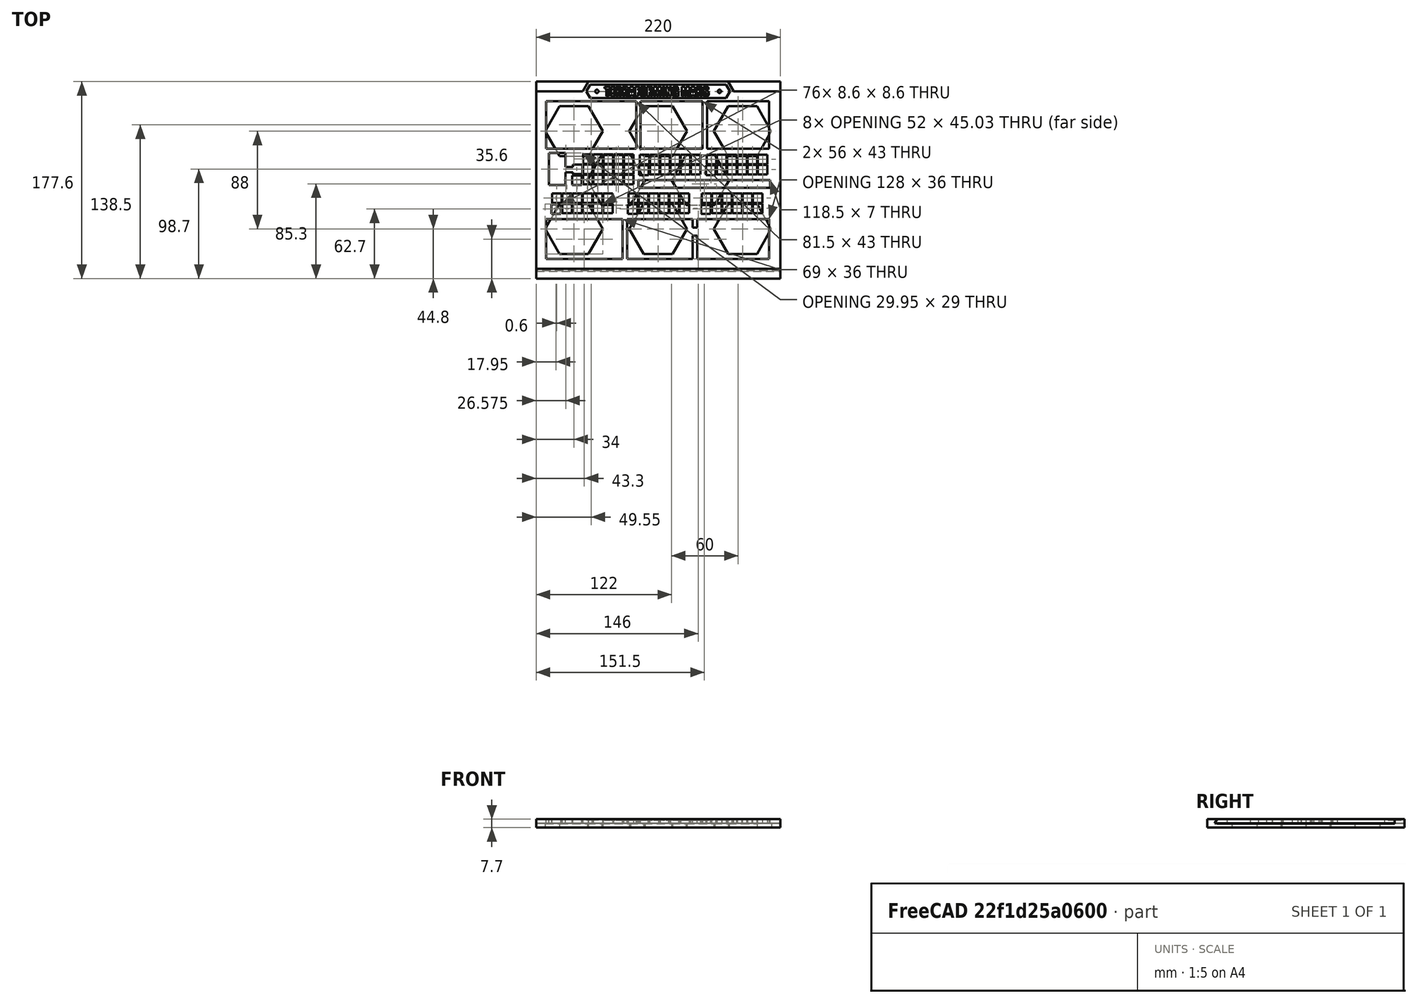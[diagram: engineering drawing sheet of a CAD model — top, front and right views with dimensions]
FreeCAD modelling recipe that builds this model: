
FCSTD DOCUMENT  (FreeCAD 0.21R33668 +26 (Git))
Label: overlay-full-v6
License: All rights reserved
LicenseURL: https://en.wikipedia.org/wiki/All_rights_reserved
objects: Sketcher::SketchObject×11, PartDesign::Pad×9, PartDesign::Pocket×5, Part::Feature×2, Part::Part2DObjectPython×2, PartDesign::Body×2, Mesh::Feature×1, Part::Refine×1, PartDesign::FeatureBase×1, Part::Extrusion×1
note: 48 computed .brp shape members not serialized (recipe doc carries the construction recipe); baked Part::Feature solids carry a one-line shape summary decoded from their .brp

FEATURE [Mesh::Feature] Terraforming_Mars_overlay
FEATURE [Part::Feature] Terraforming_Mars_overlay001
  shape: bbox 208 x 148 x 3.7 mm, 1736 faces, 0 solids (baked)
FEATURE [Part::Feature] Terraforming_Mars_overlay001_solid  label="Terraforming_Mars_overlay001 (Solid)"
  shape: bbox 208 x 148 x 3.7 mm, 1736 faces (baked)
FEATURE [Part::Refine] Terraforming_Mars_overlay001_solid001  label="Terraforming_Mars_overlay001 (Solid)001"
  Source = -> Terraforming_Mars_overlay001_solid
FEATURE [PartDesign::FeatureBase] BaseFeature
  BaseFeature = -> Terraforming_Mars_overlay001_solid001
FEATURE [Sketcher::SketchObject] Sketch
  ExternalGeometry = -> [BaseFeature]
  FullyConstrained = true
  MapMode = 5
  Placement = pos=(0,0,3.7) rot=(0,0,1;0rad)
  Support = -> [BaseFeature]
  sketch-geometry (8):
    g0: LineSegment StartX=6 StartY=154 StartZ=0 EndX=214 EndY=154 EndZ=0
    g1: LineSegment StartX=214 StartY=154 StartZ=0 EndX=214 EndY=6 EndZ=0
    g2: LineSegment StartX=214 StartY=6 StartZ=0 EndX=6 EndY=6 EndZ=0
    g3: LineSegment StartX=6 StartY=6 StartZ=0 EndX=6 EndY=154 EndZ=0
    g4: LineSegment StartX=0 StartY=160 StartZ=0 EndX=220 EndY=160 EndZ=0
    g5: LineSegment StartX=220 StartY=160 StartZ=0 EndX=220 EndY=0 EndZ=0
    g6: LineSegment StartX=220 StartY=0 StartZ=0 EndX=0 EndY=0 EndZ=0
    g7: LineSegment StartX=0 StartY=0 StartZ=0 EndX=0 EndY=160 EndZ=0
  constraints (22):
    c: Coincident(g0,g1)
    c: Coincident(g1,g2)
    c: Coincident(g2,g3)
    c: Coincident(g3,g0)
    c: Horizontal(g0)
    c: Horizontal(g2)
    c: Vertical(g1)
    c: Vertical(g3)
    c: Coincident(g0,g-3)
    c: Coincident(g1,g-4)
    c: Coincident(g4,g5)
    c: Coincident(g5,g6)
    c: Coincident(g6,g7)
    c: Coincident(g7,g4)
    c: Horizontal(g4)
    c: Horizontal(g6)
    c: Vertical(g5)
    c: Vertical(g7)
    c: DistanceX(g4,g0) = 6
    c: DistanceX(g0,g4) = 6
    c: DistanceY(g0,g4) = 6
    c: DistanceY(g5,g1) = 6
FEATURE [PartDesign::Pad] Pad
  BaseFeature = -> BaseFeature
  Direction = (0,0,1)
  Length = 10
  Length2 = 10
  Profile = -> Sketch
  ReferenceAxis = -> Sketch [N_Axis]
  Type = 3
  UpToFace = -> BaseFeature [Face1]
FEATURE [Sketcher::SketchObject] Sketch001
  ExternalGeometry = -> [Pad]
  FullyConstrained = true
  MapMode = 5
  Placement = pos=(0,0,3.7) rot=(0,0,1;0rad)
  Support = -> [Pad]
  sketch-geometry (5):
    g0: GeomPoint X=110 Y=160 Z=0
    g1: LineSegment StartX=42 StartY=160 StartZ=0 EndX=47.0807 EndY=168.8 EndZ=0
    g2: LineSegment StartX=47.0807 StartY=168.8 StartZ=0 EndX=172.919 EndY=168.8 EndZ=0
    g3: LineSegment StartX=172.919 StartY=168.8 StartZ=0 EndX=178 EndY=160 EndZ=0
    g4: LineSegment StartX=178 StartY=160 StartZ=0 EndX=42 EndY=160 EndZ=0
  constraints (13):
    c: Symmetric(g-3,g-3,g0)
    c: Coincident(g1,g2)
    c: Horizontal(g2)
    c: Coincident(g2,g3)
    c: Coincident(g3,g4)
    c: Coincident(g4,g1)
    c: Angle(g1,g4,g1) = 2.0944
    c: Angle(g4,g3,g3) = 2.0944
    c: DistanceY(g1,g1) = 8.8
    c: PointOnObject(g1,g-3)
    c: DistanceX(g-3,g1) = 42
    c: DistanceX(g3,g-3) = 42
    c: PointOnObject(g3,g-3)
FEATURE [PartDesign::Pad] Pad001
  BaseFeature = -> Pad
  Direction = (0,0,1)
  Length = 10
  Length2 = 10
  Profile = -> Sketch001
  ReferenceAxis = -> Sketch001 [N_Axis]
  Type = 3
  UpToFace = -> Pad [Face2]
FEATURE [Sketcher::SketchObject] Sketch002
  ExternalGeometry = -> [Pad001]
  FullyConstrained = true
  MapMode = 5
  Placement = pos=(0,0,3.7) rot=(0,0,1;0rad)
  Support = -> [Pad001]
  sketch-geometry (7):
    g0: GeomPoint X=110 Y=160 Z=0
    g1: LineSegment StartX=45.2332 StartY=160 StartZ=0 EndX=48.6973 EndY=166 EndZ=0
    g2: LineSegment StartX=48.6973 StartY=166 StartZ=0 EndX=171.303 EndY=166 EndZ=0
    g3: LineSegment StartX=171.303 StartY=166 StartZ=0 EndX=174.767 EndY=160 EndZ=0
    g4: LineSegment StartX=174.767 StartY=160 StartZ=0 EndX=171.303 EndY=154 EndZ=0
    g5: LineSegment StartX=171.303 StartY=154 StartZ=0 EndX=48.6973 EndY=154 EndZ=0
    g6: LineSegment StartX=48.6973 StartY=154 StartZ=0 EndX=45.2332 EndY=160 EndZ=0
  constraints (17):
    c: Symmetric(g-4,g-4,g0)
    c: PointOnObject(g1,g-4)
    c: Coincident(g1,g2)
    c: Horizontal(g2)
    c: Coincident(g2,g3)
    c: PointOnObject(g3,g-4)
    c: Coincident(g3,g4)
    c: PointOnObject(g4,g-5)
    c: Coincident(g4,g5)
    c: Coincident(g5,g6)
    c: Coincident(g6,g1)
    c: Parallel(g1,g-6)
    c: Symmetric(g5,g1,g-4)
    c: Symmetric(g4,g2,g-4)
    c: Parallel(g3,g-7)
    c: Distance(g1,g-6) = 2.8
    c: Distance(g2,g-7) = 2.8
FEATURE [PartDesign::Pocket] Pocket
  BaseFeature = -> Pad001
  Direction = (0,0,-1)
  Length = 1
  Length2 = 5
  Profile = -> Sketch002
  ReferenceAxis = -> Sketch002 [N_Axis]
  Type = 0
FEATURE [Part::Part2DObjectPython] ShapeString  # Draft 2D object (typed FeaturePython)
  FontFile = <path>
  MakeFace = true
  Placement = pos=(61.7,155.5,2.7) rot=(0,0,1;0rad)
  Size = 9
  String = TERRAFORMING MARS
  Tracking = 0
FEATURE [Sketcher::SketchObject] Sketch003
  ExternalGeometry = -> [Pocket]
  FullyConstrained = true
  MapMode = 5
  Placement = pos=(0,0,2.7) rot=(0,0,1;0rad)
  Support = -> [Pocket]
  sketch-geometry (3):
    g0: LineSegment StartX=45.2332 StartY=160 StartZ=0 EndX=174.767 EndY=160 EndZ=0
    g1: Circle CenterX=54.7332 CenterY=160 CenterZ=0 NormalX=0 NormalY=0 NormalZ=1 AngleXU=0 Radius=1.5
    g2: Circle CenterX=165.267 CenterY=160 CenterZ=0 NormalX=0 NormalY=0 NormalZ=1 AngleXU=0 Radius=1.5
  constraints (8):
    c: Coincident(g0,g-3)
    c: Coincident(g0,g-4)
    c: PointOnObject(g1,g0)
    c: PointOnObject(g2,g0)
    c: Diameter(g2) = 3
    c: Diameter(g1) = 3
    c: DistanceX(g0,g1) = 9.5
    c: DistanceX(g2,g0) = 9.5
FEATURE [PartDesign::Pad] Pad002
  BaseFeature = -> Pocket
  Direction = (0,0,1)
  Length = 1
  Length2 = 10
  Profile = -> Sketch003
  ReferenceAxis = -> Sketch003 [N_Axis]
  Type = 0
FEATURE [PartDesign::Pad] Pad003
  BaseFeature = -> Pad002
  Direction = (0,-1,0)
  Length = 2
  Length2 = 10
  Profile = -> Pad002 [Face352]
  Type = 0
FEATURE [Sketcher::SketchObject] Sketch004
  ExternalGeometry = -> [Pad003]
  FullyConstrained = true
  MapMode = 5
  Placement = pos=(220,0,0) rot=(0.57735,0.57735,0.57735;2.0944rad)
  Support = -> [Pad003]
  sketch-geometry (3):
    g0: LineSegment StartX=0 StartY=3.7 StartZ=0 EndX=-2 EndY=0 EndZ=0
    g1: LineSegment StartX=-2 StartY=0 StartZ=0 EndX=-2 EndY=3.7 EndZ=0
    g2: LineSegment StartX=-2 StartY=3.7 StartZ=0 EndX=0 EndY=3.7 EndZ=0
  constraints (6):
    c: Coincident(g-4,g0)
    c: Coincident(g0,g-3)
    c: Coincident(g0,g1)
    c: Coincident(g1,g-4)
    c: Coincident(g1,g2)
    c: Coincident(g2,g0)
FEATURE [PartDesign::Pocket] Pocket001
  BaseFeature = -> Pad003
  Direction = (-1,0,0)
  Length = 5
  Length2 = 5
  Profile = -> Sketch004
  ReferenceAxis = -> Sketch004 [N_Axis]
  Type = 1
FEATURE [PartDesign::Body] Body  label="Front"
  BaseFeature = -> Terraforming_Mars_overlay001_solid001
  Group = -> [BaseFeature,Sketch,Pad,Sketch001,Pad001,Sketch002,Pocket,Sketch003,Pad002,Pad003,Sketch004,Pocket001]
  Origin = -> Origin
  Tip = -> Pocket001
FEATURE [Part::Extrusion] Extrude  label="Text"
  Base = -> ShapeString
  Dir = (0,0,1)
  DirMode = 2
  FaceMakerClass = Part::FaceMakerBullseye
  LengthFwd = 1
  LengthRev = 0
  Solid = false
  Symmetric = false
FEATURE [Sketcher::SketchObject] Sketch005
  FullyConstrained = true
  MapMode = 5
  Support = -> [XY_Plane001]
  sketch-geometry (4):
    g0: LineSegment StartX=0 StartY=160 StartZ=0 EndX=220 EndY=160 EndZ=0
    g1: LineSegment StartX=220 StartY=160 StartZ=0 EndX=220 EndY=0 EndZ=0
    g2: LineSegment StartX=220 StartY=0 StartZ=0 EndX=0 EndY=0 EndZ=0
    g3: LineSegment StartX=0 StartY=0 StartZ=0 EndX=0 EndY=160 EndZ=0
  constraints (12):
    c: Coincident(g0,g1)
    c: Coincident(g1,g2)
    c: Coincident(g2,g3)
    c: Coincident(g3,g0)
    c: Horizontal(g0)
    c: Horizontal(g2)
    c: Vertical(g1)
    c: Vertical(g3)
    c: PointOnObject(g1,g-1)
    c: PointOnObject(g0,g-2)
    c: DistanceX(g0,g0) = 220
    c: DistanceY(g1,g1) = 160
FEATURE [PartDesign::Pad] Pad004
  Direction = (0,0,1)
  Length = 4
  Length2 = 10
  Profile = -> Sketch005
  ReferenceAxis = -> Sketch005 [N_Axis]
  Reversed = true
  Type = 0
FEATURE [PartDesign::Pad] Pad005
  BaseFeature = -> Pad004
  Direction = (0,-1,0)
  Length = 8.8
  Length2 = 10
  Profile = -> Pad004 [Face3]
  Type = 0
FEATURE [PartDesign::Pad] Pad006
  BaseFeature = -> Pad005
  Direction = (0,0,1)
  Length = 3.7
  Length2 = 10
  Profile = -> Pad005 [Face8]
  Type = 0
FEATURE [Sketcher::SketchObject] Sketch006
  ExternalGeometry = -> [Pad006]
  FullyConstrained = true
  MapMode = 5
  Placement = pos=(0,0,0) rot=(0.57735,-0.57735,-0.57735;2.0944rad)
  Support = -> [Pad006]
  sketch-geometry (4):
    g0: LineSegment StartX=0 StartY=0 StartZ=0 EndX=2.1 EndY=0 EndZ=0
    g1: LineSegment StartX=0.1 StartY=3.7 StartZ=0 EndX=2.1 EndY=0 EndZ=0
    g2: LineSegment StartX=0 StartY=3.7 StartZ=0 EndX=0 EndY=0 EndZ=0
    g3: LineSegment StartX=0.1 StartY=3.7 StartZ=0 EndX=0 EndY=3.7 EndZ=0
  constraints (10):
    c: Coincident(g-1,g0)
    c: PointOnObject(g0,g-1)
    c: Coincident(g1,g0)
    c: DistanceX(g0,g0) = 2.1
    c: PointOnObject(g1,g-3)
    c: Coincident(g2,g-3)
    c: Coincident(g2,g0)
    c: Coincident(g3,g1)
    c: Coincident(g3,g2)
    c: DistanceX(g3,g3) = 0.1
FEATURE [PartDesign::Pocket] Pocket002
  BaseFeature = -> Pad006
  Direction = (1,0,0)
  Length = 5
  Length2 = 5
  Profile = -> Sketch006
  ReferenceAxis = -> Sketch006 [N_Axis]
  Type = 1
FEATURE [PartDesign::Pad] Pad007
  BaseFeature = -> Pocket002
  Direction = (0,1,0)
  Length = 8.8
  Length2 = 10
  Profile = -> Pocket002 [Face1]
  Type = 0
FEATURE [Sketcher::SketchObject] Sketch007
  ExternalGeometry = -> [Pad007]
  FullyConstrained = true
  MapMode = 5
  Placement = pos=(0,0,0) rot=(0.57735,-0.57735,-0.57735;2.0944rad)
  Support = -> [Pad007]
  sketch-geometry (3):
    g0: LineSegment StartX=4.63784 StartY=3.7 StartZ=0 EndX=8.8 EndY=-4 EndZ=0
    g1: LineSegment StartX=8.8 StartY=-4 StartZ=0 EndX=8.8 EndY=3.7 EndZ=0
    g2: LineSegment StartX=8.8 StartY=3.7 StartZ=0 EndX=4.63784 EndY=3.7 EndZ=0
  constraints (7):
    c: PointOnObject(g0,g-3)
    c: Coincident(g0,g-6)
    c: Coincident(g1,g0)
    c: Coincident(g1,g-5)
    c: Coincident(g2,g1)
    c: Coincident(g2,g0)
    c: Parallel(g0,g-4)
FEATURE [Sketcher::SketchObject] Sketch008
  ExternalGeometry = -> [Pad007]
  FullyConstrained = true
  MapMode = 5
  Support = -> [Pad007]
  sketch-geometry (12):
    g0: LineSegment StartX=0 StartY=160 StartZ=0 EndX=42 EndY=160 EndZ=0
    g1: LineSegment StartX=42 StartY=160 StartZ=0 EndX=47.0807 EndY=168.8 EndZ=0
    g2: LineSegment StartX=0 StartY=168.8 StartZ=0 EndX=46.9652 EndY=168.8 EndZ=0
    g3: LineSegment StartX=46.9652 StartY=168.8 StartZ=0 EndX=41.9423 EndY=160.1 EndZ=0
    g4: LineSegment StartX=41.9423 StartY=160.1 StartZ=0 EndX=0 EndY=160.1 EndZ=0
    g5: LineSegment StartX=0 StartY=160.1 StartZ=0 EndX=0 EndY=168.8 EndZ=0
    g6: LineSegment StartX=172.919 StartY=168.8 StartZ=0 EndX=178 EndY=160 EndZ=0
    g7: LineSegment StartX=178 StartY=160 StartZ=0 EndX=220 EndY=160 EndZ=0
    g8: LineSegment StartX=173.035 StartY=168.8 StartZ=0 EndX=220 EndY=168.8 EndZ=0
    g9: LineSegment StartX=220 StartY=168.8 StartZ=0 EndX=220 EndY=160.1 EndZ=0
    g10: LineSegment StartX=220 StartY=160.1 StartZ=0 EndX=178.058 EndY=160.1 EndZ=0
    g11: LineSegment StartX=178.058 StartY=160.1 StartZ=0 EndX=173.035 EndY=168.8 EndZ=0
  constraints (34):
    c: Coincident(g-4,g0)
    c: PointOnObject(g0,g-4)
    c: Coincident(g0,g1)
    c: PointOnObject(g1,g-3)
    c: DistanceX(g0,g0) = 42
    c: Angle(g-4,g1,g0) = 1.0472
    c: Coincident(g-3,g2)
    c: PointOnObject(g2,g-3)
    c: Coincident(g2,g3)
    c: Coincident(g3,g4)
    c: PointOnObject(g4,g-2)
    c: Horizontal(g4)
    c: Coincident(g4,g5)
    c: Coincident(g5,g2)
    c: Parallel(g3,g1)
    c: Distance(g4,g0) = 0.1
    c: Distance(g2,g1) = 0.1
    c: PointOnObject(g6,g-3)
    c: PointOnObject(g6,g-4)
    c: Coincident(g7,g6)
    c: Coincident(g7,g-5)
    c: DistanceX(g7,g7) = 42
    c: Angle(g6,g-4,g6) = 1.0472
    c: PointOnObject(g8,g-3)
    c: Coincident(g8,g-5)
    c: Coincident(g8,g9)
    c: PointOnObject(g9,g-5)
    c: Coincident(g9,g10)
    c: Horizontal(g10)
    c: Coincident(g10,g11)
    c: Coincident(g11,g8)
    c: Distance(g8,g6) = 0.1
    c: Parallel(g11,g6)
    c: Distance(g9,g7) = 0.1
FEATURE [PartDesign::Pad] Pad008
  BaseFeature = -> Pad007
  Direction = (0,0,1)
  Length = 3.7
  Length2 = 10
  Profile = -> Sketch008
  ReferenceAxis = -> Sketch008 [N_Axis]
  Type = 0
FEATURE [Sketcher::SketchObject] Sketch009
  ExternalGeometry = -> [Pad008]
  FullyConstrained = true
  MapMode = 5
  Support = -> [Pad008]
  sketch-geometry (4):
    g0: LineSegment StartX=0 StartY=0 StartZ=0 EndX=220 EndY=0 EndZ=0
    g1: LineSegment StartX=220 StartY=0 StartZ=0 EndX=220 EndY=160 EndZ=0
    g2: LineSegment StartX=220 StartY=160 StartZ=0 EndX=0 EndY=160 EndZ=0
    g3: LineSegment StartX=0 StartY=160 StartZ=0 EndX=0 EndY=0 EndZ=0
  constraints (10):
    c: Coincident(g0,g1)
    c: Coincident(g1,g2)
    c: Coincident(g2,g3)
    c: Coincident(g3,g0)
    c: Horizontal(g0)
    c: Horizontal(g2)
    c: Vertical(g1)
    c: Vertical(g3)
    c: Coincident(g0,g-5)
    c: Coincident(g1,g-4)
FEATURE [PartDesign::Pocket] Pocket003
  BaseFeature = -> Pad008
  Direction = (0,0,-1)
  Length = 0.3
  Length2 = 5
  Profile = -> Sketch009
  ReferenceAxis = -> Sketch009 [N_Axis]
  Type = 0
FEATURE [Part::Part2DObjectPython] ShapeString001  # Draft 2D object (typed FeaturePython)
  FontFile = <path>
  MakeFace = true
  Placement = pos=(12.35,20,0) rot=(0,0,1;1e-06rad)
  Size = 120
  String = T M
  Tracking = 0
FEATURE [Sketcher::SketchObject] Sketch010
  ExternalGeometry = -> [Pocket003]
  FullyConstrained = true
  MapMode = 5
  Placement = pos=(0,0,-0.3) rot=(0,0,1;0rad)
  Support = -> [Pocket003]
  sketch-geometry (64):
    g0: LineSegment StartX=220 StartY=124 StartZ=0 EndX=0 EndY=124 EndZ=0
    g1: LineSegment StartX=220 StartY=80 StartZ=0 EndX=0 EndY=80 EndZ=0
    g2: LineSegment StartX=220 StartY=36 StartZ=0 EndX=0 EndY=36 EndZ=0
    g3: LineSegment StartX=98 StartY=80 StartZ=0 EndX=85 EndY=102.517 EndZ=0
    g4: LineSegment StartX=85 StartY=102.517 StartZ=0 EndX=59 EndY=102.517 EndZ=0
    g5: LineSegment StartX=59 StartY=102.517 StartZ=0 EndX=46 EndY=80 EndZ=0
    g6: LineSegment StartX=46 StartY=80 StartZ=0 EndX=59 EndY=57.4833 EndZ=0
    g7: LineSegment StartX=59 StartY=57.4833 StartZ=0 EndX=85 EndY=57.4833 EndZ=0
    g8: LineSegment StartX=85 StartY=57.4833 StartZ=0 EndX=98 EndY=80 EndZ=0
    g9: Circle CenterX=72 CenterY=80 CenterZ=0 NormalX=0 NormalY=0 NormalZ=1 AngleXU=0 Radius=26
    g10: LineSegment StartX=60 StartY=124 StartZ=0 EndX=47 EndY=146.517 EndZ=0
    g11: LineSegment StartX=47 StartY=146.517 StartZ=0 EndX=21 EndY=146.517 EndZ=0
    g12: LineSegment StartX=21 StartY=146.517 StartZ=0 EndX=8 EndY=124 EndZ=0
    g13: LineSegment StartX=8 StartY=124 StartZ=0 EndX=21 EndY=101.483 EndZ=0
    g14: LineSegment StartX=21 StartY=101.483 StartZ=0 EndX=47 EndY=101.483 EndZ=0
    g15: LineSegment StartX=47 StartY=101.483 StartZ=0 EndX=60 EndY=124 EndZ=0
    g16: Circle CenterX=34 CenterY=124 CenterZ=0 NormalX=0 NormalY=0 NormalZ=1 AngleXU=0 Radius=26
    g17: LineSegment StartX=136 StartY=124 StartZ=0 EndX=123 EndY=146.517 EndZ=0
    g18: LineSegment StartX=123 StartY=146.517 StartZ=0 EndX=97 EndY=146.517 EndZ=0
    g19: LineSegment StartX=97 StartY=146.517 StartZ=0 EndX=84 EndY=124 EndZ=0
    g20: LineSegment StartX=84 StartY=124 StartZ=0 EndX=97 EndY=101.483 EndZ=0
    g21: LineSegment StartX=97 StartY=101.483 StartZ=0 EndX=123 EndY=101.483 EndZ=0
    g22: LineSegment StartX=123 StartY=101.483 StartZ=0 EndX=136 EndY=124 EndZ=0
    g23: Circle CenterX=110 CenterY=124 CenterZ=0 NormalX=0 NormalY=0 NormalZ=1 AngleXU=0 Radius=26
    g24: LineSegment StartX=174 StartY=80 StartZ=0 EndX=161 EndY=102.517 EndZ=0
    g25: LineSegment StartX=161 StartY=102.517 StartZ=0 EndX=135 EndY=102.517 EndZ=0
    g26: LineSegment StartX=135 StartY=102.517 StartZ=0 EndX=122 EndY=80 EndZ=0
    g27: LineSegment StartX=122 StartY=80 StartZ=0 EndX=135 EndY=57.4833 EndZ=0
    g28: LineSegment StartX=135 StartY=57.4833 StartZ=0 EndX=161 EndY=57.4833 EndZ=0
    g29: LineSegment StartX=161 StartY=57.4833 StartZ=0 EndX=174 EndY=80 EndZ=0
    g30: Circle CenterX=148 CenterY=80 CenterZ=0 NormalX=0 NormalY=0 NormalZ=1 AngleXU=0 Radius=26
    g31: LineSegment StartX=212 StartY=124 StartZ=0 EndX=199 EndY=146.517 EndZ=0
    g32: LineSegment StartX=199 StartY=146.517 StartZ=0 EndX=173 EndY=146.517 EndZ=0
    g33: LineSegment StartX=173 StartY=146.517 StartZ=0 EndX=160 EndY=124 EndZ=0
    g34: LineSegment StartX=160 StartY=124 StartZ=0 EndX=173 EndY=101.483 EndZ=0
    g35: LineSegment StartX=173 StartY=101.483 StartZ=0 EndX=199 EndY=101.483 EndZ=0
    g36: LineSegment StartX=199 StartY=101.483 StartZ=0 EndX=212 EndY=124 EndZ=0
    g37: Circle CenterX=186 CenterY=124 CenterZ=0 NormalX=0 NormalY=0 NormalZ=1 AngleXU=0 Radius=26
    g38: LineSegment StartX=34 StartY=160 StartZ=0 EndX=34 EndY=0 EndZ=0
    g39: LineSegment StartX=72 StartY=160 StartZ=0 EndX=72 EndY=0 EndZ=0
    g40: LineSegment StartX=110 StartY=160 StartZ=0 EndX=110 EndY=0 EndZ=0
    g41: LineSegment StartX=148 StartY=160 StartZ=0 EndX=148 EndY=0 EndZ=0
    g42: LineSegment StartX=186 StartY=160 StartZ=0 EndX=186 EndY=0 EndZ=0
    g43: LineSegment StartX=212 StartY=36 StartZ=0 EndX=199 EndY=58.5167 EndZ=0
    g44: LineSegment StartX=199 StartY=58.5167 StartZ=0 EndX=173 EndY=58.5167 EndZ=0
    g45: LineSegment StartX=173 StartY=58.5167 StartZ=0 EndX=160 EndY=36 EndZ=0
    g46: LineSegment StartX=160 StartY=36 StartZ=0 EndX=173 EndY=13.4833 EndZ=0
    g47: LineSegment StartX=173 StartY=13.4833 StartZ=0 EndX=199 EndY=13.4833 EndZ=0
    g48: LineSegment StartX=199 StartY=13.4833 StartZ=0 EndX=212 EndY=36 EndZ=0
    g49: Circle CenterX=186 CenterY=36 CenterZ=0 NormalX=0 NormalY=0 NormalZ=1 AngleXU=0 Radius=26
    g50: LineSegment StartX=136 StartY=36 StartZ=0 EndX=123 EndY=58.5167 EndZ=0
    g51: LineSegment StartX=123 StartY=58.5167 StartZ=0 EndX=97 EndY=58.5167 EndZ=0
    g52: LineSegment StartX=97 StartY=58.5167 StartZ=0 EndX=84 EndY=36 EndZ=0
    g53: LineSegment StartX=84 StartY=36 StartZ=0 EndX=97 EndY=13.4833 EndZ=0
    g54: LineSegment StartX=97 StartY=13.4833 StartZ=0 EndX=123 EndY=13.4833 EndZ=0
    g55: LineSegment StartX=123 StartY=13.4833 StartZ=0 EndX=136 EndY=36 EndZ=0
    g56: Circle CenterX=110 CenterY=36 CenterZ=0 NormalX=0 NormalY=0 NormalZ=1 AngleXU=0 Radius=26
    g57: LineSegment StartX=60 StartY=36 StartZ=0 EndX=47 EndY=58.5167 EndZ=0
    g58: LineSegment StartX=47 StartY=58.5167 StartZ=0 EndX=21 EndY=58.5167 EndZ=0
    g59: LineSegment StartX=21 StartY=58.5167 StartZ=0 EndX=8 EndY=36 EndZ=0
    g60: LineSegment StartX=8 StartY=36 StartZ=0 EndX=21 EndY=13.4833 EndZ=0
    g61: LineSegment StartX=21 StartY=13.4833 StartZ=0 EndX=47 EndY=13.4833 EndZ=0
    g62: LineSegment StartX=47 StartY=13.4833 StartZ=0 EndX=60 EndY=36 EndZ=0
    g63: Circle CenterX=34 CenterY=36 CenterZ=0 NormalX=0 NormalY=0 NormalZ=1 AngleXU=0 Radius=26
  constraints (168):
    c: PointOnObject(g0,g-5)
    c: Horizontal(g0)
    c: PointOnObject(g1,g-5)
    c: PointOnObject(g1,g-3)
    c: Horizontal(g1)
    c: PointOnObject(g2,g-5)
    c: PointOnObject(g2,g-2)
    c: Horizontal(g2)
    c: PointOnObject(g0,g-3)
    c: DistanceY(g0,g-4) = 36
    c: DistanceY(g1,g0) = 44
    c: DistanceY(g2,g1) = 44
    c: Coincident(g3,g4)
    c: Coincident(g4,g5)
    c: Coincident(g5,g6)
    c: Coincident(g6,g7)
    c: Coincident(g7,g8)
    c: Coincident(g8,g3)
    c: Equal(g3, g4-g8) x5
    c: PointOnObject(g3,g9)
    c: PointOnObject(g4,g9)
    c: PointOnObject(g5,g9)
    c: PointOnObject(g6,g9)
    c: PointOnObject(g7,g9)
    c: PointOnObject(g8,g9)
    c: PointOnObject(g9,g1)
    c: PointOnObject(g8,g1)
    c: Coincident(g10,g11)
    c: Coincident(g11,g12)
    c: Coincident(g12,g13)
    c: Coincident(g13,g14)
    c: Coincident(g14,g15)
    c: Coincident(g15,g10)
    c: Equal(g10, g11-g15) x5
    c: PointOnObject(g10,g16)
    c: PointOnObject(g11,g16)
    c: PointOnObject(g12,g16)
    c: PointOnObject(g13,g16)
    c: PointOnObject(g14,g16)
    c: PointOnObject(g15,g16)
    c: PointOnObject(g16,g0)
    c: PointOnObject(g15,g0)
    c: Coincident(g17,g18)
    c: Coincident(g18,g19)
    c: Coincident(g19,g20)
    c: Coincident(g20,g21)
    c: Coincident(g21,g22)
    c: Coincident(g22,g17)
    c: Equal(g17, g18-g22) x5
    c: PointOnObject(g17,g23)
    c: PointOnObject(g18,g23)
    c: PointOnObject(g19,g23)
    c: PointOnObject(g20,g23)
    c: PointOnObject(g21,g23)
    c: PointOnObject(g22,g23)
    c: PointOnObject(g23,g0)
    c: PointOnObject(g22,g0)
    c: Coincident(g24,g25)
    c: Coincident(g25,g26)
    c: Coincident(g26,g27)
    c: Coincident(g27,g28)
    c: Coincident(g28,g29)
    c: Coincident(g29,g24)
    c: Equal(g24, g25-g29) x5
    c: PointOnObject(g24,g30)
    c: PointOnObject(g25,g30)
    c: PointOnObject(g26,g30)
    c: PointOnObject(g27,g30)
    c: PointOnObject(g28,g30)
    c: PointOnObject(g29,g30)
    c: PointOnObject(g30,g1)
    c: PointOnObject(g29,g1)
    c: Coincident(g31,g32)
    c: Coincident(g32,g33)
    c: Coincident(g33,g34)
    c: Coincident(g34,g35)
    c: Coincident(g35,g36)
    c: Coincident(g36,g31)
    c: Equal(g31, g32-g36) x5
    c: PointOnObject(g31,g37)
    c: PointOnObject(g32,g37)
    c: PointOnObject(g33,g37)
    c: PointOnObject(g34,g37)
    c: PointOnObject(g35,g37)
    c: PointOnObject(g36,g37)
    c: PointOnObject(g37,g0)
    c: PointOnObject(g36,g0)
    c: PointOnObject(g38,g-4)
    c: PointOnObject(g38,g-6)
    c: Vertical(g38)
    c: PointOnObject(g39,g-4)
    c: PointOnObject(g39,g-6)
    c: Vertical(g39)
    c: PointOnObject(g40,g-4)
    c: PointOnObject(g40,g-6)
    c: Vertical(g40)
    c: PointOnObject(g41,g-4)
    c: PointOnObject(g41,g-6)
    c: Vertical(g41)
    c: PointOnObject(g42,g-4)
    c: PointOnObject(g42,g-6)
    c: Vertical(g42)
    c: DistanceX(g38,g39) = 38
    c: DistanceX(g39,g40) = 38
    c: DistanceX(g40,g41) = 38
    c: DistanceX(g41,g42) = 38
    c: DistanceX(g-4,g38) = 34
    c: PointOnObject(g16,g38)
    c: Radius(g16) = 26
    c: PointOnObject(g9,g39)
    c: Radius(g9) = 26
    c: Radius(g23) = 26
    c: Radius(g30) = 26
    c: Radius(g37) = 26
    c: PointOnObject(g30,g41)
    c: PointOnObject(g37,g42)
    c: Coincident(g43,g44)
    c: Coincident(g44,g45)
    c: Coincident(g45,g46)
    c: Coincident(g46,g47)
    c: Coincident(g47,g48)
    c: Coincident(g48,g43)
    c: Equal(g43, g44-g48) x5
    c: PointOnObject(g43,g49)
    c: PointOnObject(g44,g49)
    c: PointOnObject(g45,g49)
    c: PointOnObject(g46,g49)
    c: PointOnObject(g47,g49)
    c: PointOnObject(g48,g49)
    c: PointOnObject(g49,g2)
    c: PointOnObject(g48,g2)
    c: Coincident(g50,g51)
    c: Coincident(g51,g52)
    c: Coincident(g52,g53)
    c: Coincident(g53,g54)
    c: Coincident(g54,g55)
    c: Coincident(g55,g50)
    c: Equal(g50, g51-g55) x5
    c: PointOnObject(g50,g56)
    c: PointOnObject(g51,g56)
    c: PointOnObject(g52,g56)
    c: PointOnObject(g53,g56)
    c: PointOnObject(g54,g56)
    c: PointOnObject(g55,g56)
    c: PointOnObject(g56,g2)
    c: PointOnObject(g55,g2)
    c: Coincident(g57,g58)
    c: Coincident(g58,g59)
    c: Coincident(g59,g60)
    c: Coincident(g60,g61)
    c: Coincident(g61,g62)
    c: Coincident(g62,g57)
    c: Equal(g57, g58-g62) x5
    c: PointOnObject(g57,g63)
    c: PointOnObject(g58,g63)
    c: PointOnObject(g59,g63)
    c: PointOnObject(g60,g63)
    c: PointOnObject(g61,g63)
    c: PointOnObject(g62,g63)
    c: PointOnObject(g63,g2)
    c: PointOnObject(g62,g2)
    c: PointOnObject(g49,g42)
    c: PointOnObject(g56,g40)
    c: PointOnObject(g63,g38)
    c: Radius(g63) = 26
    c: Radius(g56) = 26
    c: Radius(g49) = 26
    c: PointOnObject(g23,g40)
FEATURE [PartDesign::Pocket] Pocket004
  BaseFeature = -> Pocket003
  Direction = (0,0,-1)
  Length = 5
  Length2 = 5
  Profile = -> Sketch010
  ReferenceAxis = -> Sketch010 [N_Axis]
  Type = 1
FEATURE [PartDesign::Body] Body001  label="Back"
  Group = -> [Sketch005,Pad004,Pad005,Pad006,Sketch006,Pocket002,Pad007,Sketch007,Sketch008,Pad008,Sketch009,Pocket003,Sketch010,Pocket004]
  Origin = -> Origin001
  Tip = -> Pocket004
note: 2 file-system paths scrubbed to <path> (originals preserved in the JSON sidecar)
